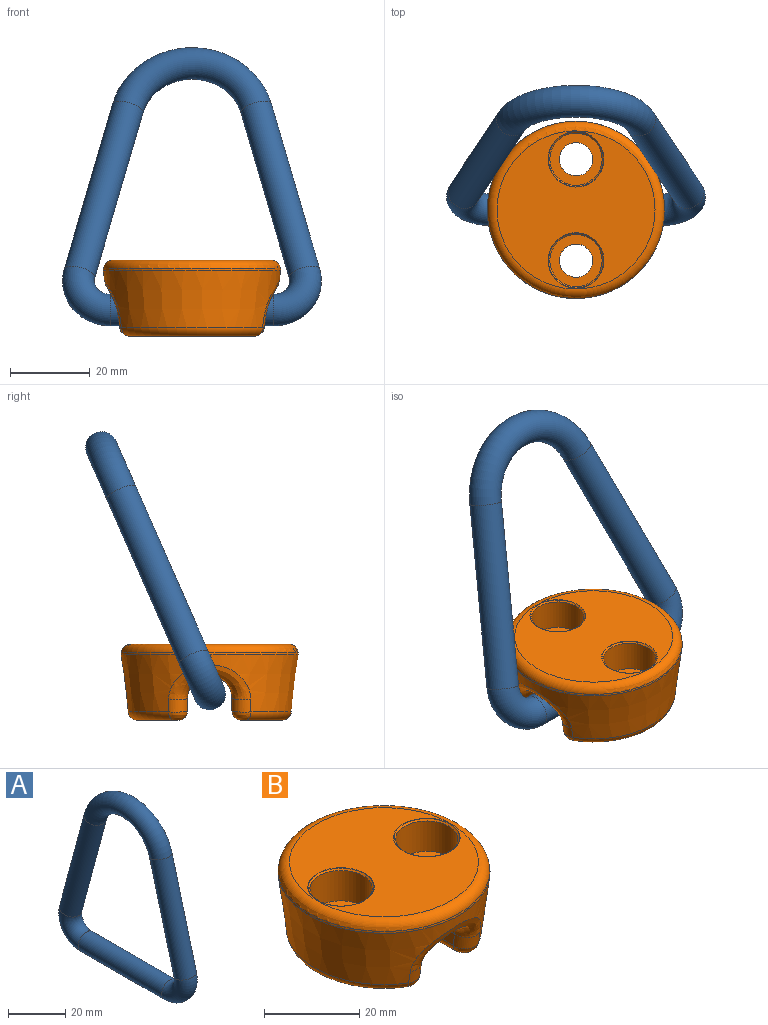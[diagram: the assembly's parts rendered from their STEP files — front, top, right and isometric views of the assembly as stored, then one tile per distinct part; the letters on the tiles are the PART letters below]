
ASSEMBLY  parts=2 mates=1
PART A: 6 faces, bbox 7.9x66.8x78.1 mm
  f0: cylinder r=3.97mm len=47.18mm, axis (0,0.26,0.97), area 1164.9mm2, adj f1,f5
  f1: torus R=7.94mm, axis (-1,0,0), area 362.7mm2, adj f0,f2
  f2: cylinder r=3.97mm len=41.05mm, axis (0,-1,0), area 1023.6mm2, adj f1,f3
  f3: torus R=7.94mm, axis (-1,0,0), area 362.7mm2, adj f2,f4
  f4: cylinder r=3.97mm len=47.18mm, axis (0,0.26,-0.97), area 1164.9mm2, adj f3,f5
  f5: torus R=16.67mm, axis (1,0,0), area 1088.2mm2, adj f0,f4
PART B: 44 faces, bbox 48x48x32 mm
  f0: plane 39.61x39.61mm, normal (0,0,1), area 926.8mm2, adj f22,f42,f43
  f1: cylinder r=5.56mm len=30.74mm, axis (0,1,0), area 274.6mm2, adj f6,f7,f9,f12,f32,f33,f34,f35
  f2: plane 31.44x10.14mm, normal (0,0,-1), area 170mm2, adj f14,f15,f16,f17,f39
  f3: cone r=22.23mm half-angle=7deg, axis (0,0,-1), area 63.1mm2, adj f4,f22
  f4: cone r=22.23mm half-angle=7deg, axis (0,0,1), area 1520.3mm2, adj f3,f8,f9,f10,f11,f12,f13,f16
  f5: plane 31.44x10.14mm, normal (0,0,-1), area 170mm2, adj f18,f19,f20,f21,f38
  f6: plane 30.74x3.18mm, normal (1,0,0), area 96.2mm2, adj f1,f8,f13,f15
  f7: plane 30.74x3.18mm, normal (-1,0,0), area 96.2mm2, adj f1,f10,f11,f20
  f8: bspline ~26.1x8.53mm, area 21mm2, adj f4,f6,f9,f17
  f9: bspline ~20.6x10.49mm, area 128mm2, adj f1,f4,f8,f10
  f10: bspline ~32.03x9.37mm, area 20.9mm2, adj f4,f7,f9,f21
  f11: bspline ~26.1x8.53mm, area 21mm2, adj f4,f7,f12,f18
  f12: bspline ~20.6x10.49mm, area 128mm2, adj f1,f4,f11,f13
  f13: bspline ~32.03x9.37mm, area 20.9mm2, adj f4,f6,f12,f14
  f14: bspline ~5.36x3.34mm, area 16.6mm2, adj f2,f13,f15,f16
  f15: cylinder r=2.39mm len=29.84mm, axis (0,-1,0), area 111.9mm2, adj f2,f6,f14,f17
  f16: torus R=18.09mm, axis (0,0,-1), area 140.7mm2, adj f2,f4,f14,f17
  f17: bspline ~5.37x3.89mm, area 16.6mm2, adj f2,f8,f15,f16
  f18: bspline ~5.37x3.89mm, area 16.6mm2, adj f5,f11,f19,f20
  f19: torus R=18.09mm, axis (0,0,-1), area 140.7mm2, adj f4,f5,f18,f21
  f20: cylinder r=2.39mm len=29.84mm, axis (0,1,0), area 111.9mm2, adj f5,f7,f18,f21
  f21: bspline ~5.36x3.34mm, area 16.6mm2, adj f5,f10,f19,f20
  f22: torus R=19.81mm, axis (0,0,1), area 460.6mm2, adj f0,f3
  f23: cylinder r=6.54mm len=13.08mm, axis (0,0,1), area 320.5mm2, adj f24,f41
  f24: plane 13.08x13.08mm, normal (0,0,1), area 79.9mm2, adj f23,f25
  f25: cylinder r=4.17mm len=10.49mm, axis (0,0,1), area 274.6mm2, adj f24,f38
  f26: cylinder r=6.54mm len=13.08mm, axis (0,0,1), area 320.5mm2, adj f27,f40
  f27: plane 13.08x13.08mm, normal (0,0,1), area 79.9mm2, adj f26,f28
  f28: cylinder r=4.17mm len=10.49mm, axis (0,0,1), area 274.6mm2, adj f27,f39
  f29: cylinder r=5.56mm len=14.86mm, axis (0,-1,0), area 273.5mm2, adj f30,f31,f32,f37
  f30: torus R=5.05mm, axis (0,-1,0), area 7.2mm2, adj f29,f34,f36
  f31: torus R=5.05mm, axis (0,-1,0), area 7.2mm2, adj f29,f33,f35
  f32: cylinder r=0.51mm len=14.86mm, axis (0,1,0), area 1.3mm2, adj f1,f29,f33,f34
  f33: bspline ~5.89x5.61mm, area 5mm2, adj f1,f31,f32,f35
  f34: bspline ~6.89x5.61mm, area 5mm2, adj f1,f30,f32,f36
  f35: bspline ~6.89x5.61mm, area 5mm2, adj f1,f31,f33,f37
  f36: bspline ~6.89x5.61mm, area 5mm2, adj f1,f30,f34,f37
  f37: cylinder r=0.51mm len=14.86mm, axis (0,-1,0), area 1.3mm2, adj f1,f29,f35,f36
  f38: cone r=4.55mm half-angle=45deg, axis (0,0,-1), area 14.7mm2, adj f5,f25
  f39: cone r=4.55mm half-angle=45deg, axis (0,0,-1), area 14.7mm2, adj f2,f28
  f40: cone r=6.54mm half-angle=45deg, axis (0,0,1), area 20.5mm2, adj f26,f43
  f41: cone r=6.54mm half-angle=45deg, axis (0,0,1), area 20.5mm2, adj f23,f42
  f42: torus R=6.97mm, axis (0,0,1), area 4.3mm2, adj f0,f41
  f43: torus R=6.97mm, axis (0,0,1), area 4.3mm2, adj f0,f40
PLACE A rot(axis=(-0.2,-0.2,-0.96),92.4deg) t=(0,4.15,16.03)mm
PLACE B rot(axis=(0,0,1),90deg) t=(0,0,16.51)mm fixed
MATE revolute A.f2 <-> B.f29  axis (-1,0,0) through (0,0,6.58)mm
